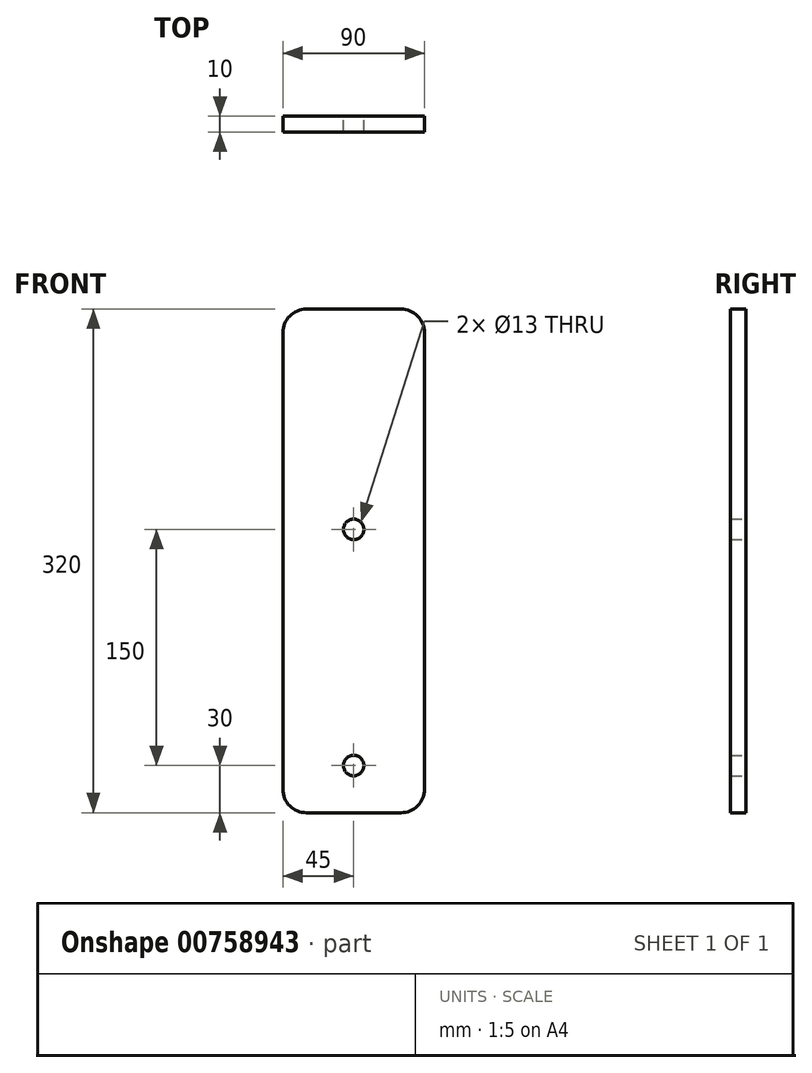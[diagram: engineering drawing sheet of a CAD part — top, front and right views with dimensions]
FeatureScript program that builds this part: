
annotation { "Feature Type Name" : "Feature", "Feature Type Description" : "" }
export const myFeature = defineFeature(function(context is Context, id is Id, definition is map)
    precondition{}
    {
        {
            var Q0;
            Q0=qCreatedBy(makeId("Front.planeOp"),FACE);
            var sketch = newSketch(context, id + "F0", { "sketchPlane" : qUnion([Q0])});
            skLineSegment(sketch, "E0.bottom", {"start": v(15, 0) * mm, "end": v(75, 0) * mm});
            skLineSegment(sketch, "E0.top", {"start": v(15, 320) * mm, "end": v(75, 320) * mm});
            skLineSegment(sketch, "E0.left", {"start": v(0, 15) * mm, "end": v(0, 305) * mm});
            skLineSegment(sketch, "E0.right", {"start": v(90, 15) * mm, "end": v(90, 305) * mm});
            skCircle(sketch, "E1", {"center": v(45, 180) * mm, "radius": 6.5 * mm});
            skCircle(sketch, "E2", {"center": v(45, 30) * mm, "radius": 6.5 * mm});
            skPoint(sketch, "E3.visualSharp", {"position": v(0, 320) * mm});
            skArc(sketch, "E3.filletArc", {"start": v(15, 320) * mm, "mid": v(4.4, 315.6) * mm, "end": v(0, 305) * mm});
            skPoint(sketch, "E4.visualSharp", {"position": v(90, 320) * mm});
            skArc(sketch, "E4.filletArc", {"start": v(90, 305) * mm, "mid": v(85.6, 315.6) * mm, "end": v(75, 320) * mm});
            skPoint(sketch, "E5.visualSharp", {"position": v(90, 0) * mm});
            skArc(sketch, "E5.filletArc", {"start": v(75, 0) * mm, "mid": v(85.6, 4.4) * mm, "end": v(90, 15) * mm});
            skPoint(sketch, "E6.visualSharp", {"position": v(0, 0) * mm});
            skArc(sketch, "E6.filletArc", {"start": v(0, 15) * mm, "mid": v(4.4, 4.4) * mm, "end": v(15, 0) * mm});
            skSolve(sketch);
        }
        {
            var Q0;
            Q0=makeQuery(id+"F0.imprint","IMPRINT",FACE,{"disambiguationData":[TD([[makeQuery(id+"F0.imprint","IMPRINT",EDGE,{"derivedFrom":sQuery(id+"F0.wireOp",EDGE,"E0.bottom")}),1.0]])]});
            extrude(context, id + "F1", {"entities" : qUnion([Q0]), "depth" : 10 * mm, "offsetDistance" : 25 * mm});
        }
    });
